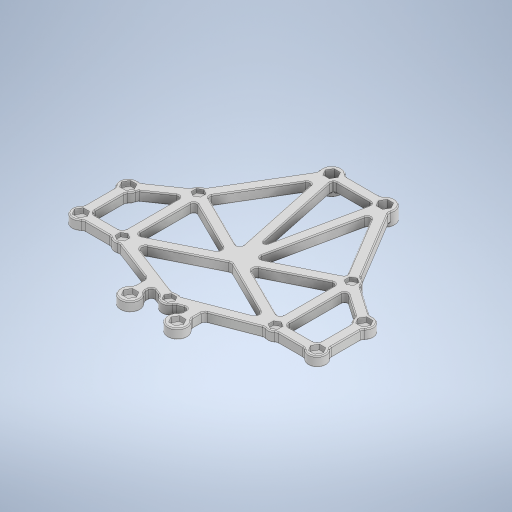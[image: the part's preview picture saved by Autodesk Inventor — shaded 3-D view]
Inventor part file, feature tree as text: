
AUTODESK INVENTOR PART (.ipt)
format: ipt  version: 2024.2 (Build 282272000, 272)  size: 1,574,912 bytes
history: native  units: mm
features: projected_geometry x67, extrude x8, sketch x6, fillet x5, hole x2
ambient origin geometry x8: Origin, YZ Plane, XZ Plane, XY Plane, X Axis, Y Axis, Z Axis, Center Point
bodies: Solid1 (feature_tree)
feature tree (88):
  sketch  "Sketch1"  dims[d0=4.8mm d9=5.6mm]
  extrude  "Extrusion1"  Depth=5.6mm
  sketch  "Sketch2"  dims[d10=24.0mm d11=9.0mm]
  extrude  "Extrusion2"  Depth=9.0mm
  extrude  "Extrusion3"  Depth=5.0mm
  extrude  "Extrusion4"  Depth=2.5mm
  extrude  "Extrusion5"  Depth=2.5mm
  hole  "Hole1"  [1 undecoded]
  hole  "Hole2"  [1 undecoded]
  fillet  "Fillet1"  Radius=2.5mm
  fillet  "Fillet2"  Radius=2.5mm
  fillet  "Fillet3"  Radius=5.0mm
  fillet  "Fillet7"  Radius=2.5mm
  fillet  "Fillet8"  Radius=5.0mm
  extrude  "Extrusion6"  Depth=2.5mm
  extrude  "Extrusion7"  Depth=2.5mm
  extrude  "Extrusion8"  Depth=2.5mm
  projected_geometry  "Projected Loop1"
  projected_geometry  "Projected Loop2"
  projected_geometry  "Projected Loop3"
  projected_geometry  "Projected Loop4"
  projected_geometry  "Projected Loop5"
  projected_geometry  "Projected Loop6"
  projected_geometry  "Projected Loop7"
  projected_geometry  "Projected Loop8"
  projected_geometry  "Projected Loop9"
  projected_geometry  "Projected Loop10"
  projected_geometry  "Projected Loop11"
  projected_geometry  "Projected Loop12"
  projected_geometry  "Projected Loop13"
  projected_geometry  "Projected Loop14"
  projected_geometry  "Projected Loop15"
  projected_geometry  "Projected Loop16"
  projected_geometry  "Projected Loop17"
  projected_geometry  "Projected Loop18"
  projected_geometry  "Projected Loop19"
  projected_geometry  "Projected Loop20"
  projected_geometry  "Projected Loop21"
  projected_geometry  "Projected Loop22"
  projected_geometry  "Projected Loop23"
  projected_geometry  "Projected Loop24"
  projected_geometry  "Projected Loop25"
  projected_geometry  "Projected Loop26"
  projected_geometry  "Projected Loop27"
  projected_geometry  "Projected Loop28"
  projected_geometry  "Projected Loop29"
  projected_geometry  "Projected Loop30"
  projected_geometry  "Projected Loop31"
  projected_geometry  "Projected Loop32"
  projected_geometry  "Projected Loop33"
  projected_geometry  "Projected Loop34"
  projected_geometry  "Projected Loop35"
  projected_geometry  "Projected Loop36"
  projected_geometry  "Projected Loop37"
  projected_geometry  "Projected Loop38"
  projected_geometry  "Projected Loop39"
  projected_geometry  "Projected Loop40"
  projected_geometry  "Projected Loop41"
  projected_geometry  "Projected Loop42"
  projected_geometry  "Projected Loop43"
  projected_geometry  "Projected Loop44"
  projected_geometry  "Projected Loop45"
  projected_geometry  "Projected Loop46"
  projected_geometry  "Projected Loop47"
  projected_geometry  "Projected Loop48"
  projected_geometry  "Projected Loop49"
  projected_geometry  "Projected Loop50"
  projected_geometry  "Projected Loop51"
  projected_geometry  "Projected Loop52"
  projected_geometry  "Projected Loop53"
  projected_geometry  "Projected Loop54"
  projected_geometry  "Projected Loop55"
  projected_geometry  "Projected Loop56"
  projected_geometry  "Projected Loop57"
  projected_geometry  "Projected Loop58"
  projected_geometry  "Projected Loop59"
  projected_geometry  "Projected Loop60"
  projected_geometry  "Projected Loop61"
  projected_geometry  "Projected Loop62"
  projected_geometry  "Projected Loop63"
  projected_geometry  "Projected Loop64"
  projected_geometry  "Projected Loop65"
  projected_geometry  "Projected Loop66"
  projected_geometry  "Projected Loop67"
  sketch  "Sketch3"  dims[d16=120.0mm d17=5.0mm]
  sketch  "Sketch4"  dims[d18=2.5mm d22=5.0mm]
  sketch  "Sketch6"  dims[d23=2.5mm d24=2.5mm]
  sketch  "Sketch7"  dims[d25=2.5mm d26=2.5mm d27=5.0mm d28=2.5mm d29=2.5mm d30=5.0mm d31=2.5mm d32=5.0mm d33=2.5mm d34=2.5mm d35=2.5mm d36=5.0mm d37=2.5mm d42=27.0mm d48=2.5mm d51=12.0mm d52=8.0mm d53=10.0mm d55=8.0mm d56=5.0mm d57=2.5mm d58=24.0mm d59=5.0mm d60=0.0mm d61=1.9mm d62=0.0mm d63=2.5mm d64=0.0mm d65=3.5mm d66=6.0mm d67=4.0mm d68=2.0mm d69=90.0deg d70=6.0mm d71=0.0mm d72=5.25mm d73=6.0mm d74=4.0mm d75=2.0mm d76=90.0deg d77=1.0mm d78=0.0mm d79=5.0mm d80=0.0mm d81=2.0mm d82=2.0mm d83=1.5mm d90=96.0mm d91=5.0mm d92=2.5mm d95=2.5mm d96=2.5mm d97=2.5mm d98=5.0mm d100=2.0mm d101=0.0mm d102=5.0mm d103=15.0mm d104=2.5mm d105=2.5mm d106=2.5mm d107=5.0mm d108=5.0mm d109=2.5mm d110=42.0mm d127=73.0mm d128=60.0mm d129=0.5mm d130=0.0mm d131=0.2mm d132=0.0mm d133=0.2mm d134=0.0mm d135=5.0mm d136=2.5mm d137=5.0mm d138=2.5mm d139=8.0mm d140=1.0mm d141=0.5mm d84=0.0mm d85=0.0mm d86=0.0mm d87=0.0mm]
note: 2 required parameter values undecoded (feature->parameter linkage not recoverable at this tier; creation-order binding heuristic only, values carry confidence <= 0.55)
